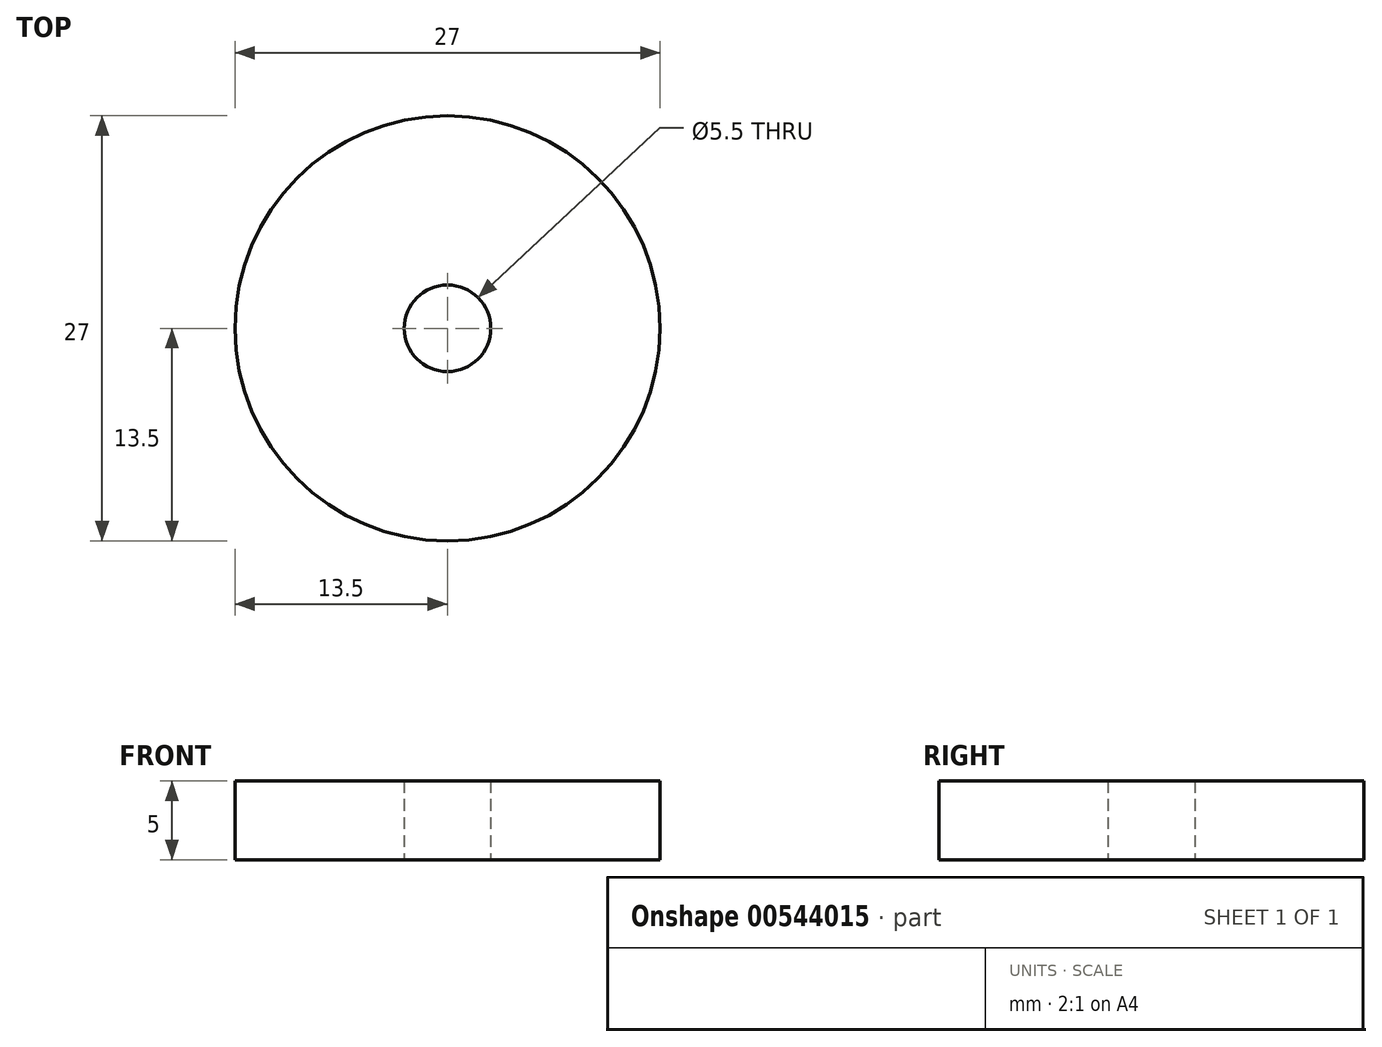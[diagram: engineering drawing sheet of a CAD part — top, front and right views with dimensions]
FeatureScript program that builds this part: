
annotation { "Feature Type Name" : "Feature", "Feature Type Description" : "" }
export const myFeature = defineFeature(function(context is Context, id is Id, definition is map)
    precondition{}
    {
        {
            var Q0;
            Q0=qCreatedBy(makeId("Top.planeOp"),FACE);
            var sketch = newSketch(context, id + "F0", { "sketchPlane" : qUnion([Q0])});
            skCircle(sketch, "E0", {"center": v(0, 0) * mm, "radius": 13.5 * mm});
            skCircle(sketch, "E1", {"center": v(0, 0) * mm, "radius": 2.75 * mm});
            skSolve(sketch);
        }
        {
            var Q0;
            Q0 = qSketchRegion(id + "F0", true);
            extrude(context, id + "F1", {"entities" : qUnion([Q0]), "depth" : 5 * mm, "offsetDistance" : 25 * mm});
        }
    });
